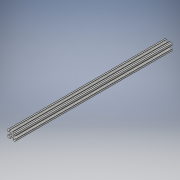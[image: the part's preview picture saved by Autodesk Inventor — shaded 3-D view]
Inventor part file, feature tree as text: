
AUTODESK INVENTOR PART (.ipt)
format: ipt  version: 2018 (Build 220112000, 112)  size: 204,800 bytes
history: native  units: in
note: dims shown in document units (in); Inventor stores cm internally (conversion verified against a paired STEP export)
features: extrude x1, sketch x1
ambient origin geometry x8: Origin, YZ Plane, XZ Plane, XY Plane, X Axis, Y Axis, Z Axis, Center Point
bodies: Solid1 (feature_tree)
feature tree (2):
  extrude  "Extrusion1"  [1 undecoded]
  sketch  "Sketch1"  dims[d0=20.0in d1=0.0in]
note: 1 required parameter value undecoded (feature->parameter linkage not recoverable at this tier; creation-order binding heuristic only, values carry confidence <= 0.55)
